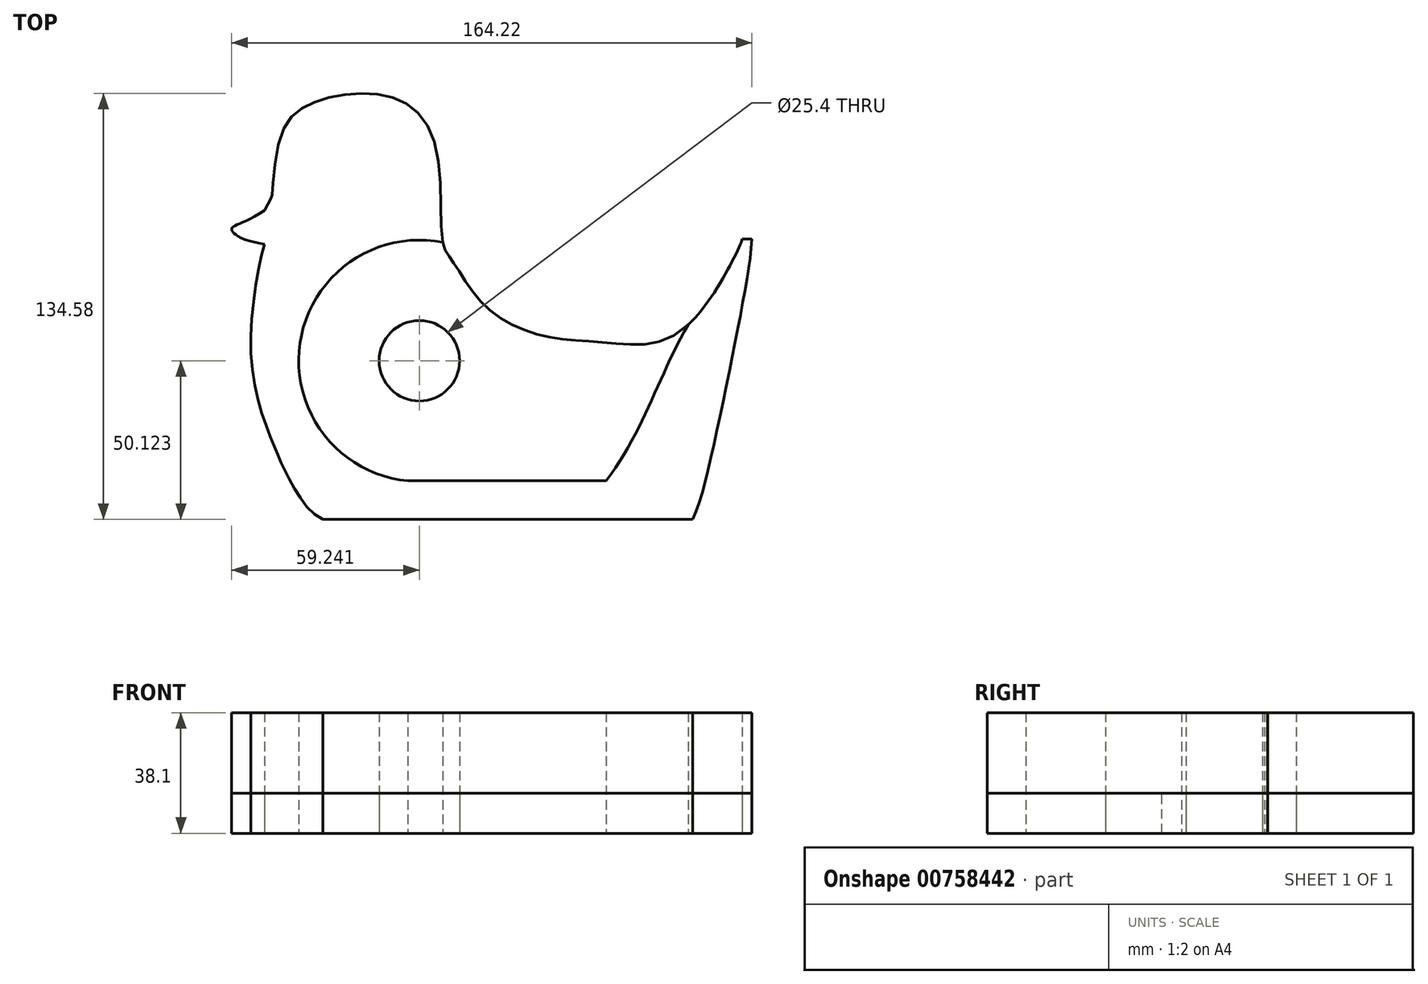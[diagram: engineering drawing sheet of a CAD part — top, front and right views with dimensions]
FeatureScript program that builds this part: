
annotation { "Feature Type Name" : "Feature", "Feature Type Description" : "" }
export const myFeature = defineFeature(function(context is Context, id is Id, definition is map)
    precondition{}
    {
        {
            var Q0;
            Q0=qCreatedBy(makeId("Top.planeOp"),FACE);
            var sketch = newSketch(context, id + "F0", { "sketchPlane" : qUnion([Q0])});
            skCircle(sketch, "E0", {"center": v(-14.03, -5.7) * mm, "radius": 12.7 * mm});
            skLineSegment(sketch, "E1", {"start": v(-44.49, -55.83) * mm, "end": v(72.26, -55.83) * mm});
            skFitSpline(sketch, "E2", {"points": [v(-44.49, -55.83) * mm, v(-55.07, -43.15) * mm, v(-60.15, -32.02) * mm, v(-67.05, -5.46) * mm, v(-62.93, 31.06) * mm], "startDerivative": vector(-63.66, 27.08) * mm, "endDerivative": vector(21.06, 76.3) * mm});
            skFitSpline(sketch, "E3", {"points": [v(-62.93, 31.06) * mm, v(-73.26, 35.94) * mm, v(-62.93, 41.75) * mm], "startDerivative": vector(-45.77, 7.12) * mm, "endDerivative": vector(40.33, 26.21) * mm});
            skFitSpline(sketch, "E4", {"points": [v(-62.93, 41.75) * mm, v(-60.52, 46.58) * mm, v(-57.74, 65.26) * mm, v(-49.46, 74.92) * mm, v(-33.24, 78.71) * mm, v(-17.72, 75.26) * mm, v(-8.4, 59.74) * mm, v(-6.63, 31.67) * mm], "startDerivative": vector(84.74, 169.47) * mm, "endDerivative": vector(18.59, -98.7) * mm});
            skFitSpline(sketch, "E5", {"points": [v(-6.63, 31.67) * mm, v(-3.23, 25.24) * mm, v(6.48, 11.8) * mm, v(24.62, 2.29) * mm, v(45.44, 0) * mm, v(70.81, 5.62) * mm, v(87.8, 33.17) * mm, v(87.36, 32.78) * mm], "startDerivative": vector(15.4, -86.27) * mm, "endDerivative": vector(18.67, 47.85) * mm});
            skFitSpline(sketch, "E6", {"points": [v(90.95, 32.78) * mm, v(87.36, 8.98) * mm, v(78.87, -32.37) * mm, v(72.26, -55.83) * mm], "startDerivative": vector(-4.65, -67.53) * mm, "endDerivative": vector(-24.22, -52.72) * mm});
            skArc(sketch, "E7", {"start": v(-6.63, 31.67) * mm, "mid": v(-51.73, -0.2) * mm, "end": v(-17.63, -43.64) * mm});
            skLineSegment(sketch, "E8", {"start": v(87.9, 32.78) * mm, "end": v(90.95, 32.78) * mm});
            skPoint(sketch, "E9", {"position": v(23.14, 2.67) * mm});
            skPoint(sketch, "E10", {"position": v(-17.63, -43.64) * mm});
            skFitSpline(sketch, "E11", {"points": [v(-17.63, -43.64) * mm, v(44.94, -43.64) * mm], "startDerivative": vector(57.97, 0) * mm, "endDerivative": vector(57.97, 0) * mm});
            skFitSpline(sketch, "E12", {"points": [v(44.94, -43.64) * mm, v(70.81, 5.62) * mm], "startDerivative": vector(35.86, 47.2) * mm, "endDerivative": vector(28.8, 49.38) * mm});
            skSolve(sketch);
        }
        {
            var Q0;
            Q0=makeQuery(id+"F0.imprint","IMPRINT",FACE,{"disambiguationData":[TD([[makeQuery(id+"F0.imprint","IMPRINT",EDGE,{"derivedFrom":sQuery(id+"F0.wireOp",EDGE,"E1")}),1.0]])]});
            var Q1;
            Q1=makeQuery(id+"F0.imprint","IMPRINT",FACE,{"disambiguationData":[TD([[makeQuery(id+"F0.imprint","IMPRINT",EDGE,{"derivedFrom":sQuery(id+"F0.wireOp",EDGE,"E0")}),1.0]])]});
            extrude(context, id + "F1", {"entities" : qUnion([Q0, Q1]), "depth" : 38.1 * mm, "offsetDistance" : 25.4 * mm});
        }
        {
            var Q0;
            Q0 = qSketchRegion(id + "F0", true);
            extrude(context, id + "F2", {"entities" : qUnion([Q0]), "depth" : 12.7 * mm, "offsetDistance" : 25.4 * mm});
        }
    });
